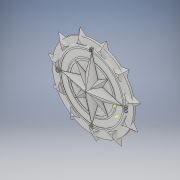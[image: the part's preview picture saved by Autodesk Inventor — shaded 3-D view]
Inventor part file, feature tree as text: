
AUTODESK INVENTOR PART (.ipt)
format: ipt  version: 2019 (Build 230136000, 136)  size: 813,568 bytes
history: native  units: mm
features: other x15, sketch x13, fillet x5, extrude x3, chamfer x1, pattern_circular x1
ambient origin geometry x8: Origin, YZ Plane, XZ Plane, XY Plane, X Axis, Y Axis, Z Axis, Center Point
bodies: Body1 (feature_tree), Body2 (feature_tree), Body3 (feature_tree), Body4 (feature_tree), Body5 (feature_tree), Body6 (feature_tree), Body7 (feature_tree), Body8 (feature_tree), Body9 (feature_tree), Body10 (feature_tree), Body11 (feature_tree), Body12 (feature_tree), Body13 (feature_tree), Body14 (feature_tree), Body15 (feature_tree), Body16 (feature_tree), Body17 (feature_tree), Body18 (feature_tree), Body19 (feature_tree), Body20 (feature_tree)
feature tree (38):
  other  "Sólido2"
  sketch  "Boceto1"  dims[d7=0.0mm d8=0.0mm d9=2.5mm d10=0.0mm d11=0.0mm d12=3.0mm]
  chamfer  "Chaflán1"  Distance=2.25mm Angle=45.0deg
  fillet  "Empalme1"  Radius=2.25mm
  fillet  "Empalme2"  Radius=2.25mm
  fillet  "Empalme3"  Radius=2.25mm
  fillet  "Empalme4"  Radius=3.75mm
  other  "Edición directa1"
  sketch  "Boceto2"  dims[d13=0.0mm d14=0.0mm d15=3.0mm d16=0.0mm d17=0.0mm d18=-3.0mm]
  sketch  "Boceto3"  dims[d19=0.0mm d20=0.0mm d21=3.0mm]
  sketch  "Boceto4"  dims[d22=0.0mm d23=0.0mm d24=3.0mm]
  sketch  "Boceto5"  dims[d25=13.5mm d26=11.25mm d27=0.0mm]
  sketch  "Boceto6"  dims[d28=2.75mm d29=0.0mm]
  other  "Edición directa2"
  extrude  "Extrusión1"  Depth=3.0mm TaperAngle=0.0deg
  sketch  "Boceto7"  dims[d30=4.0mm d31=7.85398mm d32=110.0mm d33=62.831853mm]
  extrude  "Extrusión2"  TaperAngle=0.0deg  [1 undecoded]
  pattern_circular  "Patrón circular1"  Count=11  [1 undecoded]
  sketch  "Boceto9"
  sketch  "Boceto10"
  sketch  "Boceto11"
  extrude  "Extrusión3"  Depth=50.0mm
  other  "Edición directa3"
  fillet  "Empalme5"  Radius=25.0mm
  sketch  "Boceto13"
  other  "Sólido3"
  sketch  "Boceto8"  dims[d35=2.0mm d36=0.0mm d37=50.0mm d38=10.0mm d39=10.0mm d40=25.0mm]
  sketch  "Boceto12"
  other  "Sólido1"
  other  "Sólido1:1"
  other  "Desplazar1"
  other  "Desplazar2"
  other  "Desplazar3"
  other  "Desplazar4"
  other  "Desplazar5"
  other  "Desplazar6"
  other  "Desplazar7"
  other  "Escala1"
note: 2 required parameter values undecoded (feature->parameter linkage not recoverable at this tier; creation-order binding heuristic only, values carry confidence <= 0.55)
